# Revit family: NARBUTAS - SILENT ROOM XL - Silent Room XL with melamine external
name_source: partatom
category: Furniture Systems
units: mm (PartAtom-declared; Revit-internal decimal feet)

## family parameters
Cut with Voids When Loaded = No
Host = Face
Part Type = Normal
Room Calculation Point = No
Round Connector Dimension = Use Diameter
Shared = No

## types (2) — shared parameters
Assembly Code = SILENT ROOM XL
Default Elevation = 1219 mm
Depth = 2422 mm  [stored 7.94619 ft]
Description = Acoustic Pods
Height = 2306 mm
Manufacturer = NARBUTAS
Table H = 1050 mm
TableHeight = 1050 mm
URL = https://www.narbutas.com
Voltage = 220V
Width = 3973 mm  [stored 13.0348 ft]

## per-type parameters (varying)
| type | 2D | Model |
| ARK802 3973x2422x2306 | No | ARK802 |
| ARK804 3973x2422x2306 | Yes | ARK804 |

note: [stored X ft] marks values corroborated as IEEE doubles in the binary element streams (Revit-internal decimal feet)

## geometry (parser evidence)
native form markers: Sweep x2
no freeform markers — native parametric forms only
